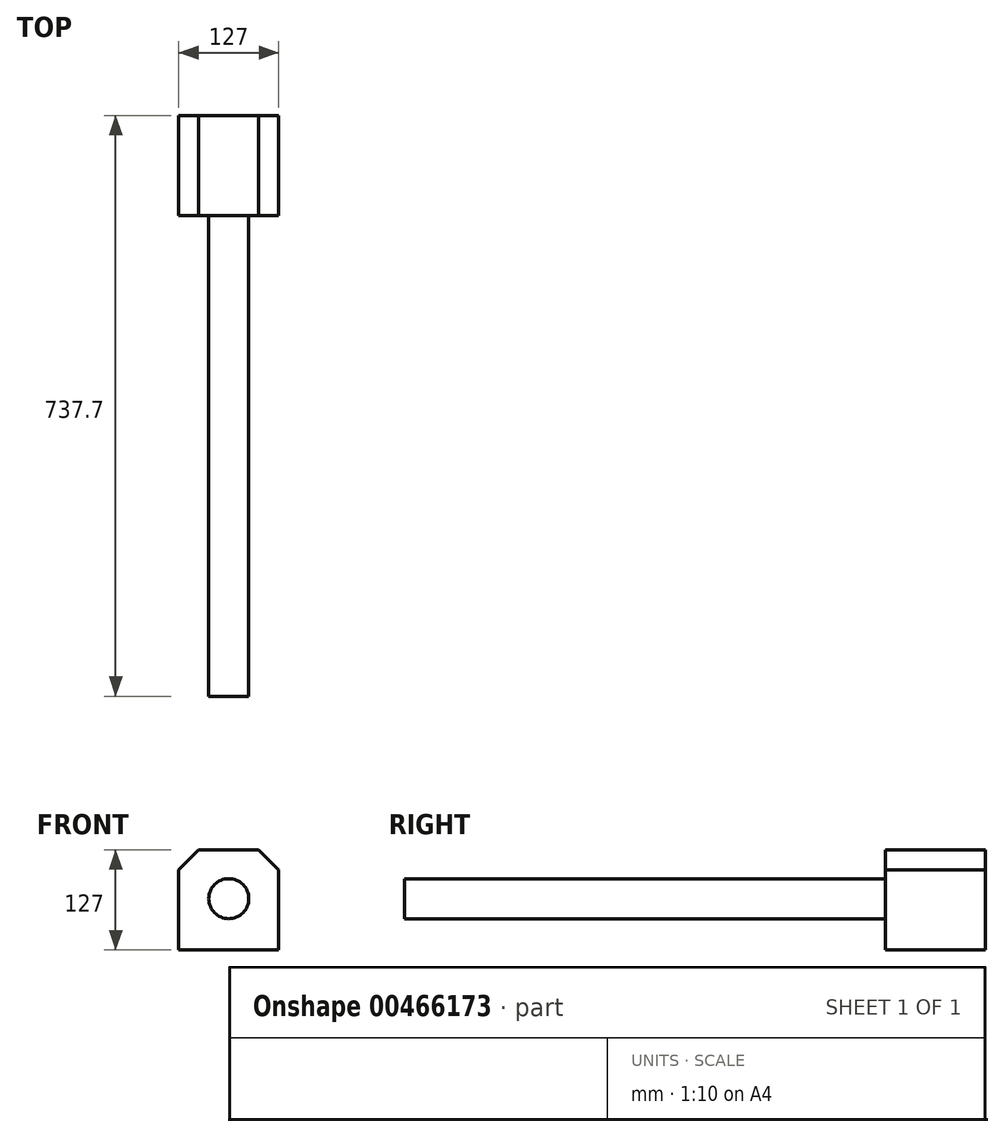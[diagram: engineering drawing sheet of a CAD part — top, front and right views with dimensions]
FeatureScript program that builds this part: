
annotation { "Feature Type Name" : "Feature", "Feature Type Description" : "" }
export const myFeature = defineFeature(function(context is Context, id is Id, definition is map)
    precondition{}
    {
        {
            var Q0;
            Q0=qCreatedBy(makeId("Front.planeOp"),FACE);
            var sketch = newSketch(context, id + "F0", { "sketchPlane" : qUnion([Q0])});
            skLineSegment(sketch, "E0.bottom", {"start": v(63.5, 61.98) * mm, "end": v(-63.5, 61.98) * mm});
            skLineSegment(sketch, "E0.top", {"start": v(63.5, -65.02) * mm, "end": v(-63.5, -65.02) * mm});
            skLineSegment(sketch, "E0.left", {"start": v(63.5, 61.98) * mm, "end": v(63.5, -65.02) * mm});
            skLineSegment(sketch, "E0.right", {"start": v(-63.5, 61.98) * mm, "end": v(-63.5, -65.02) * mm});
            skPoint(sketch, "E0.middle", {"position": v(0, -1.52) * mm});
            skSolve(sketch);
        }
        {
            var Q0;
            Q0=makeQuery(id+"F0.imprint","IMPRINT",FACE,{"disambiguationData":[TD([[makeQuery(id+"F0.imprint","IMPRINT",EDGE,{"derivedFrom":sQuery(id+"F0.wireOp",EDGE,"E0.bottom")}),1.0]])]});
            extrude(context, id + "F1", {"entities" : qUnion([Q0]), "depth" : 127 * mm});
        }
        {
            var Q0;
            Q0=makeQuery(id+"F1.opExtrude","SWEPT_EDGE",EDGE,{"disambiguationData":[OSD([sQuery(id+"F0.wireOp",EDGE,"E0.bottom"),sQuery(id+"F0.wireOp",EDGE,"E0.right")])]});
            var Q1;
            Q1=makeQuery(id+"F1.opExtrude","SWEPT_EDGE",EDGE,{"disambiguationData":[OSD([sQuery(id+"F0.wireOp",EDGE,"E0.bottom"),sQuery(id+"F0.wireOp",EDGE,"E0.left")])]});
            chamfer(context, id + "F2", {"entities" : qUnion([Q0, Q1]), "width" : 25.4 * mm, "tangentPropagation" : true});
        }
        {
            var Q0;
            Q0=makeQuery(id+"F1.opExtrude","CAP_FACE",FACE,{"disambiguationData":[OSD([sQuery(id+"F0.wireOp",EDGE,"E0.bottom"),sQuery(id+"F0.wireOp",EDGE,"E0.top"),sQuery(id+"F0.wireOp",EDGE,"E0.left"),sQuery(id+"F0.wireOp",EDGE,"E0.right")])],"isStart":false});
            var sketch = newSketch(context, id + "F3", { "sketchPlane" : qUnion([Q0])});
            skCircle(sketch, "E1", {"center": v(0, 0) * mm, "radius": 25.4 * mm});
            skSolve(sketch);
        }
        {
            var Q0;
            Q0=makeQuery(id+"F3.imprint","IMPRINT",FACE,{"disambiguationData":[TD([[makeQuery(id+"F3.imprint","IMPRINT",EDGE,{"derivedFrom":sQuery(id+"F3.wireOp",EDGE,"E1")}),1.0]])]});
            extrude(context, id + "F4", {"entities" : qUnion([Q0]), "operationType" : NewBodyOperationType.ADD, "endBound" : BoundingType.THROUGH_ALL, "depth" : 25.4 * mm});
        }
        {
            var Q0;
            Q0=makeQuery(id+"F4.opExtrude","CAP_FACE",FACE,{"disambiguationData":[OSD([sQuery(id+"F3.wireOp",EDGE,"E1")])],"isStart":false});
            extrude(context, id + "F5", {"entities" : qUnion([Q0]), "operationType" : NewBodyOperationType.ADD, "endBound" : BoundingType.THROUGH_ALL, "depth" : 25.4 * mm});
        }
    });
